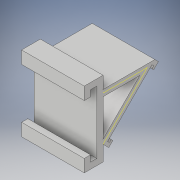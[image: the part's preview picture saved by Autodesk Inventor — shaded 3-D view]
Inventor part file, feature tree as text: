
AUTODESK INVENTOR PART (.ipt)
format: ipt  version: 2019 (Build 230136000, 136)  size: 200,704 bytes
history: native  units: mm
features: extrude x10, sketch x10, plane x1, thicken_offset x1, other x1
ambient origin geometry x8: Origin, YZ Plane, XZ Plane, XY Plane, X Axis, Y Axis, Z Axis, Center Point
bodies: Solid1 (feature_tree)
feature tree (23):
  extrude  "Extrusion1"  Depth=60.0mm
  extrude  "Extrusion2"  Depth=25.0mm
  extrude  "Extrusion3"  Depth=5.0mm
  extrude  "Extrusion4"  Depth=5.0mm
  extrude  "Extrusion5"  Depth=5.0mm
  plane  "Work Plane1"
  sketch  "Sketch7"  dims[d16=5.0mm d17=0.0mm d18=50.0mm]
  thicken_offset  "Thicken1"
  extrude  "Extrusion10"  Depth=5.0mm
  extrude  "Extrusion11"  Depth=50.0mm
  extrude  "Extrusion12"  TaperAngle=0.0deg  [1 undecoded]
  extrude  "Extrusion13"  Depth=12.325mm
  sketch  "Sketch1"  dims[d0=50.0mm d1=60.0mm]
  sketch  "Sketch2"  dims[d2=30.0mm d3=25.0mm]
  sketch  "Sketch3"  dims[d4=5.0mm d5=0.0mm d6=5.0mm]
  sketch  "Sketch4"  dims[d7=10.0mm d8=0.0mm d9=5.0mm]
  sketch  "Sketch5"  dims[d10=10.0mm d11=0.0mm d12=5.0mm]
  sketch  "Sketch6"  dims[d13=5.0mm d14=0.0mm d15=5.0mm]
  other  "Srf1"
  sketch  "Sketch13"  dims[d19=45.0deg d20=0.0mm d21=0.0mm]
  sketch  "Sketch15"  dims[d22=5.0mm d23=1.0mm d36=12.325mm]
  sketch  "Sketch19"  dims[d37=50.0mm d38=4.0mm d39=0.0mm d40=4.0mm d41=0.0mm d42=2.0mm d43=0.0mm d44=2.0mm d45=2.0mm d46=0.0mm]
  extrude  "ExtrusionSrf1"  Depth=4.0mm TaperAngle=0.0deg
note: 1 required parameter value undecoded (feature->parameter linkage not recoverable at this tier; creation-order binding heuristic only, values carry confidence <= 0.55)
